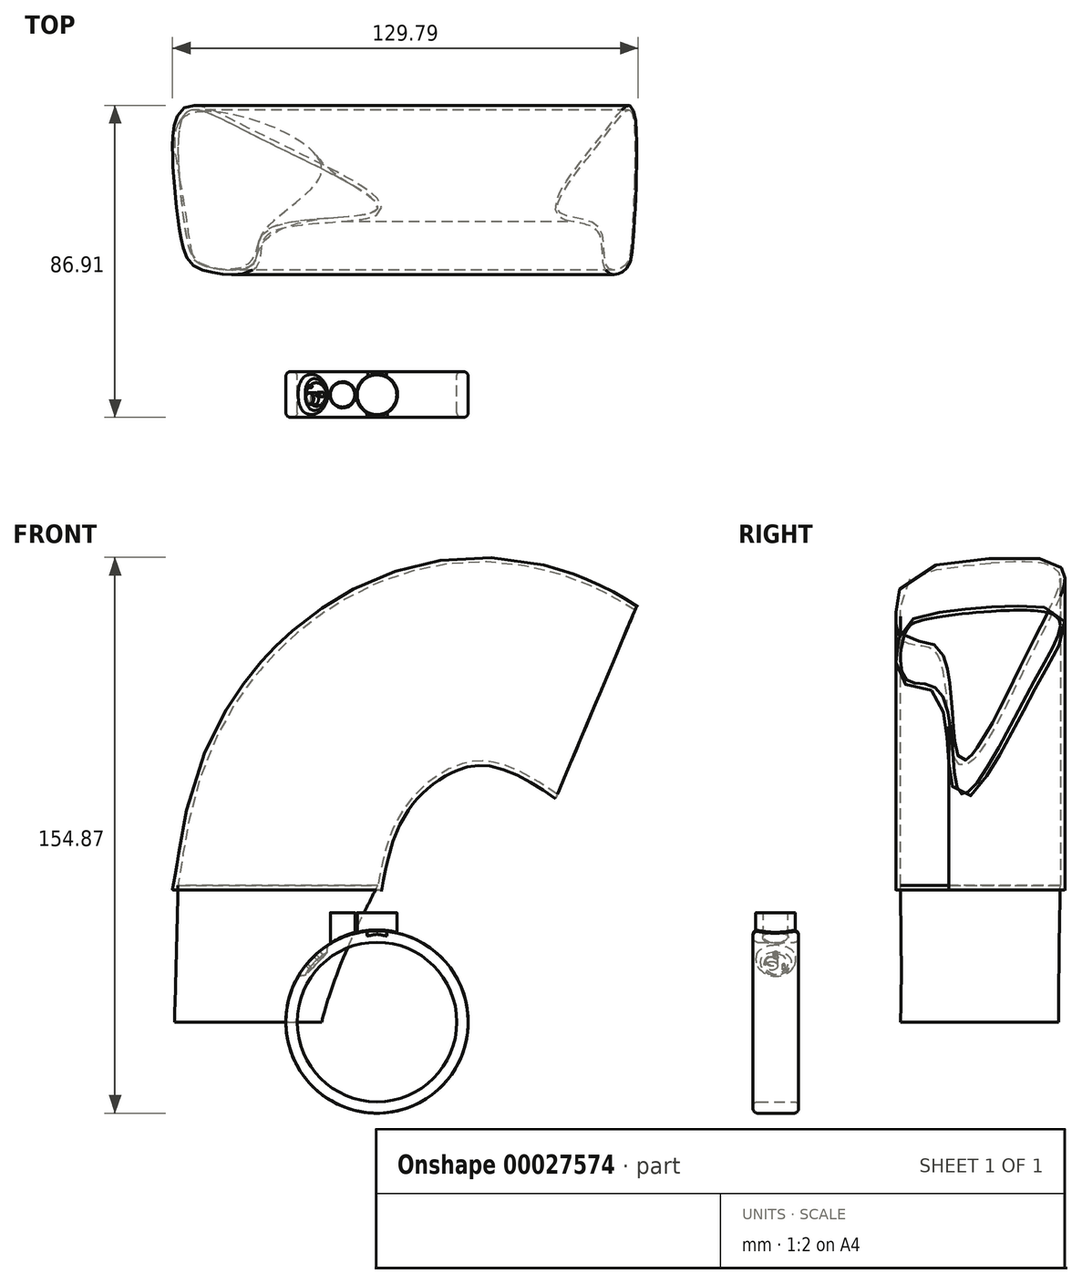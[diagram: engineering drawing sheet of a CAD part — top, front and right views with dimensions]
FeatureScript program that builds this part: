
annotation { "Feature Type Name" : "Feature", "Feature Type Description" : "" }
export const myFeature = defineFeature(function(context is Context, id is Id, definition is map)
    precondition{}
    {
        {
            var Q0;
            Q0=qCreatedBy(makeId("Front.planeOp"),FACE);
            var sketch = newSketch(context, id + "F0", { "sketchPlane" : qUnion([Q0])});
            skCircle(sketch, "E0", {"center": v(0, 0) * mm, "radius": 25.4 * mm});
            skCircle(sketch, "E1", {"center": v(0, 0) * mm, "radius": 22.23 * mm});
            skSolve(sketch);
        }
        {
            var Q0;
            Q0 = qSketchRegion(id + "F0", true);
            extrude(context, id + "F1", {"entities" : qUnion([Q0]), "depth" : 12.7 * mm});
        }
        {
            var Q0;
            Q0=qCreatedBy(makeId("Top.planeOp"),FACE);
            cPlane(context, id + "F2", {"entities" : qUnion([Q0]), "cplaneType" : CPlaneType.OFFSET, "offset" : 30.48 * mm, "width" : 152.4 * mm, "height" : 152.4 * mm});
        }
        {
            var Q0;
            Q0=qCreatedBy(id+"F2.planeOp",FACE);
            var sketch = newSketch(context, id + "F3", { "sketchPlane" : qUnion([Q0])});
            skLineSegment(sketch, "E2", {"start": v(0, -12.85) * mm, "end": v(0, 0) * mm});
            skCircle(sketch, "E3", {"center": v(0, -6.42) * mm, "radius": 5.54 * mm});
            skCircle(sketch, "E4", {"center": v(-9.6, -6.42) * mm, "radius": 3.43 * mm});
            skCircle(sketch, "E5.MirrorC", {"center": v(9.6, -6.42) * mm, "radius": 3.43 * mm});
            skSolve(sketch);
        }
        {
            var Q0;
            Q0=makeQuery(id+"F3.imprint","IMPRINT",FACE,{"disambiguationData":[TD([[makeQuery(id+"F3.imprint","IMPRINT",EDGE,{"derivedFrom":sQuery(id+"F3.wireOp",EDGE,"E4")}),1.0]])]});
            var Q1;
            {var subQ0=sQuery(id+"F3.wireOp",EDGE,"E3");var subQ1=sQuery(id+"F3.wireOp",EDGE,"E2");var subQ3=makeQuery(id+"F3.imprint","INTERSECT",VERTEX,{"disambiguationData":[OD(0.0)],"derivedFrom":[subQ1,subQ0]});Q1=makeQuery(id+"F3.imprint","IMPRINT",FACE,{"disambiguationData":[TD([[makeQuery(id+"F3.imprint","IMPRINT",EDGE,{"disambiguationData":[TD([[subQ3,-1.0]])],"derivedFrom":subQ1}),1.0]])]});}
            var Q2;
            {var subQ0=sQuery(id+"F3.wireOp",EDGE,"E3");var subQ1=sQuery(id+"F3.wireOp",EDGE,"E2");var subQ3=makeQuery(id+"F3.imprint","INTERSECT",VERTEX,{"disambiguationData":[OD(0.0)],"derivedFrom":[subQ1,subQ0]});Q2=makeQuery(id+"F3.imprint","IMPRINT",FACE,{"disambiguationData":[TD([[makeQuery(id+"F3.imprint","IMPRINT",EDGE,{"disambiguationData":[TD([[subQ3,-1.0]])],"derivedFrom":subQ1}),-1.0]])]});}
            var Q3;
            Q3=makeQuery(id+"F3.imprint","IMPRINT",FACE,{"disambiguationData":[TD([[makeQuery(id+"F3.imprint","IMPRINT",EDGE,{"derivedFrom":sQuery(id+"F3.wireOp",EDGE,"E5.MirrorC")}),-1.0]])]});
            var Q4;
            Q4=makeQuery(id+"F1.opExtrude","SWEPT_FACE",FACE,{"disambiguationData":[OSD([sQuery(id+"F0.wireOp",EDGE,"E1")])]});
            extrude(context, id + "F4", {"entities" : qUnion([Q0, Q1, Q2, Q3]), "operationType" : NewBodyOperationType.ADD, "endBound" : BoundingType.UP_TO_SURFACE, "oppositeDirection" : true, "endBoundEntityFace" : qUnion([Q4]), "depth" : 25.4 * mm});
        }
        {
            var Q0;
            Q0=makeQuery(id+"F4.opExtrude","CAP_EDGE",EDGE,{"disambiguationData":[OSD([sQuery(id+"F3.wireOp",EDGE,"E4")])],"isStart":true});
            var Q1;
            Q1=makeQuery(id+"F4.opExtrude","CAP_EDGE",EDGE,{"disambiguationData":[OSD([sQuery(id+"F3.wireOp",EDGE,"E3")])],"isStart":true});
            var Q2;
            Q2=makeQuery(id+"F4.opExtrude","CAP_EDGE",EDGE,{"disambiguationData":[OSD([sQuery(id+"F3.wireOp",EDGE,"E5.MirrorC")])],"isStart":true});
            fillet(context, id + "F5", {"entities" : qUnion([Q0, Q1, Q2]), "radius" : 0.13 * mm, "tangentPropagation" : true, "allowEdgeOverflow" : false});
        }
        {
            var Q0;
            Q0=makeQuery(id+"F4.boolean.opBoolean","INTERSECT",EDGE,{"derivedFrom":[makeQuery(id+"F1.opExtrude","SWEPT_FACE",FACE,{"disambiguationData":[OSD([sQuery(id+"F0.wireOp",EDGE,"E0")])]}),makeQuery(id+"F4.opExtrude","SWEPT_FACE",FACE,{"disambiguationData":[OSD([sQuery(id+"F3.wireOp",EDGE,"E4")])]})]});
            var Q1;
            Q1=makeQuery(id+"F4.boolean.opBoolean","INTERSECT",EDGE,{"derivedFrom":[makeQuery(id+"F1.opExtrude","SWEPT_FACE",FACE,{"disambiguationData":[OSD([sQuery(id+"F0.wireOp",EDGE,"E0")])]}),makeQuery(id+"F4.opExtrude","SWEPT_FACE",FACE,{"disambiguationData":[OSD([sQuery(id+"F3.wireOp",EDGE,"E3")])]})]});
            var Q2;
            Q2=makeQuery(id+"F4.boolean.opBoolean","INTERSECT",EDGE,{"derivedFrom":[makeQuery(id+"F1.opExtrude","SWEPT_FACE",FACE,{"disambiguationData":[OSD([sQuery(id+"F0.wireOp",EDGE,"E0")])]}),makeQuery(id+"F4.opExtrude","SWEPT_FACE",FACE,{"disambiguationData":[OSD([sQuery(id+"F3.wireOp",EDGE,"E5.MirrorC")])]})]});
            chamfer(context, id + "F6", {"entities" : qUnion([Q0, Q1, Q2]), "width" : 0.25 * mm, "tangentPropagation" : true});
        }
        {
            var Q0;
            Q0=makeQuery(id+"F1.opExtrude","CAP_EDGE",EDGE,{"disambiguationData":[OSD([sQuery(id+"F0.wireOp",EDGE,"E0")])],"isStart":false});
            var Q1;
            Q1=makeQuery(id+"F1.opExtrude","CAP_EDGE",EDGE,{"disambiguationData":[OSD([sQuery(id+"F0.wireOp",EDGE,"E1")])],"isStart":false});
            var Q2;
            Q2=makeQuery(id+"F1.opExtrude","CAP_EDGE",EDGE,{"disambiguationData":[OSD([sQuery(id+"F0.wireOp",EDGE,"E1")])],"isStart":true});
            var Q3;
            Q3=makeQuery(id+"F1.opExtrude","CAP_EDGE",EDGE,{"disambiguationData":[OSD([sQuery(id+"F0.wireOp",EDGE,"E0")])],"isStart":true});
            fillet(context, id + "F7", {"entities" : qUnion([Q0, Q1, Q2, Q3]), "radius" : 1.27 * mm, "tangentPropagation" : true, "allowEdgeOverflow" : false});
        }
        {
            var Q0;
            Q0=qCreatedBy(makeId("Front.planeOp"),FACE);
            var sketch = newSketch(context, id + "F8", { "sketchPlane" : qUnion([Q0])});
            skLineSegment(sketch, "E6", {"start": v(-13.03, 30.35) * mm, "end": v(-28.36, 14.3) * mm});
            skSolve(sketch);
        }
        {
            var Q0;
            Q0=sQuery(id+"F8.wireOp",EDGE,"E6");
            cPlane(context, id + "F9", {"entities" : qUnion([Q0]), "cplaneType" : CPlaneType.LINE_ANGLE, "offset" : 152.4 * mm, "angle" : 90 * degree, "width" : 152.4 * mm, "height" : 152.4 * mm});
        }
        {
            var Q0;
            Q0=qCreatedBy(id+"F9.planeOp",FACE);
            var sketch = newSketch(context, id + "F10", { "sketchPlane" : qUnion([Q0])});
            skCircle(sketch, "E7", {"center": v(6.35, 0) * mm, "radius": 4.4 * mm});
            skCircle(sketch, "E8", {"center": v(6.35, 0) * mm, "radius": 3.62 * mm});
            skCircle(sketch, "E9", {"center": v(6.34, 2.52) * mm, "radius": 0.64 * mm});
            skCircle(sketch, "E10", {"center": v(4.12, -2.02) * mm, "radius": 0.34 * mm});
            skCircle(sketch, "E11", {"center": v(7.5, -0.73) * mm, "radius": 1.69 * mm});
            skSolve(sketch);
        }
        {
            var Q0;
            Q0=makeQuery(id+"F10.imprint","IMPRINT",FACE,{"disambiguationData":[TD([[makeQuery(id+"F10.imprint","IMPRINT",EDGE,{"derivedFrom":sQuery(id+"F10.wireOp",EDGE,"E7")}),1.0]])]});
            var Q1;
            Q1=makeQuery(id+"F10.imprint","IMPRINT",FACE,{"disambiguationData":[TD([[makeQuery(id+"F10.imprint","IMPRINT",EDGE,{"derivedFrom":sQuery(id+"F10.wireOp",EDGE,"E8")}),1.0]])]});
            extrude(context, id + "F11", {"entities" : qUnion([Q0, Q1]), "operationType" : NewBodyOperationType.REMOVE, "oppositeDirection" : true, "depth" : 6.97 * mm});
        }
        {
            var Q0;
            Q0=makeQuery(id+"F11.boolean.opBoolean","INTERSECT",EDGE,{"derivedFrom":[makeQuery(id+"F1.opExtrude","SWEPT_FACE",FACE,{"disambiguationData":[OSD([sQuery(id+"F0.wireOp",EDGE,"E0")])]}),makeQuery(id+"F11.opExtrude","SWEPT_FACE",FACE,{"disambiguationData":[OSD([sQuery(id+"F10.wireOp",EDGE,"E7")])]})]});
            chamfer(context, id + "F12", {"entities" : qUnion([Q0]), "width" : 1.27 * mm, "tangentPropagation" : true});
        }
        {
            var Q0;
            Q0=makeQuery(id+"F11.boolean.opBoolean","COPY",EDGE,{"derivedFrom":makeQuery(id+"F11.opExtrude","CAP_EDGE",EDGE,{"disambiguationData":[OSD([sQuery(id+"F10.wireOp",EDGE,"E7")])],"isStart":false})});
            fillet(context, id + "F13", {"entities" : qUnion([Q0]), "radius" : 1.27 * mm, "tangentPropagation" : true, "allowEdgeOverflow" : false});
        }
        {
            var Q0;
            Q0=makeQuery(id+"F11.boolean.opBoolean","INTERSECT",EDGE,{"derivedFrom":[makeQuery(id+"F1.opExtrude","SWEPT_FACE",FACE,{"disambiguationData":[OSD([sQuery(id+"F0.wireOp",EDGE,"E0")])]}),makeQuery(id+"F11.opExtrude","SWEPT_FACE",FACE,{"disambiguationData":[OSD([sQuery(id+"F10.wireOp",EDGE,"E11")])]})]});
            var Q1;
            Q1=makeQuery(id+"F11.boolean.opBoolean","INTERSECT",EDGE,{"derivedFrom":[makeQuery(id+"F1.opExtrude","SWEPT_FACE",FACE,{"disambiguationData":[OSD([sQuery(id+"F0.wireOp",EDGE,"E0")])]}),makeQuery(id+"F11.opExtrude","SWEPT_FACE",FACE,{"disambiguationData":[OSD([sQuery(id+"F10.wireOp",EDGE,"E9")])]})]});
            var Q2;
            Q2=makeQuery(id+"F11.boolean.opBoolean","INTERSECT",EDGE,{"derivedFrom":[makeQuery(id+"F1.opExtrude","SWEPT_FACE",FACE,{"disambiguationData":[OSD([sQuery(id+"F0.wireOp",EDGE,"E0")])]}),makeQuery(id+"F11.opExtrude","SWEPT_FACE",FACE,{"disambiguationData":[OSD([sQuery(id+"F10.wireOp",EDGE,"E10")])]})]});
            fillet(context, id + "F14", {"entities" : qUnion([Q0, Q1, Q2]), "radius" : 0.13 * mm, "tangentPropagation" : true, "allowEdgeOverflow" : false});
        }
        {
            var Q0;
            Q0=qCreatedBy(makeId("Top.planeOp"),FACE);
            var sketch = newSketch(context, id + "F15", { "sketchPlane" : qUnion([Q0])});
            skFitSpline(sketch, "E12", {"points": [v(-54.97, 53.36) * mm, v(-51.94, 34.59) * mm, v(-48.9, 29.84) * mm, v(-34.87, 29.84) * mm, v(-31.46, 39.14) * mm, v(-15.53, 57.53) * mm, v(-52.32, 71.75) * mm, v(-54.97, 53.36) * mm]});
            skSolve(sketch);
        }
        {
            var Q0;
            Q0=qCreatedBy(makeId("Top.planeOp"),FACE);
            cPlane(context, id + "F16", {"entities" : qUnion([Q0]), "cplaneType" : CPlaneType.OFFSET, "offset" : 38.1 * mm, "width" : 152.4 * mm, "height" : 152.4 * mm});
        }
        {
            var Q0;
            Q0=qCreatedBy(id+"F16.planeOp",FACE);
            var sketch = newSketch(context, id + "F17", { "sketchPlane" : qUnion([Q0])});
            skFitSpline(sketch, "E13", {"points": [v(-55.1, 53.7) * mm, v(-52.2, 33.8) * mm, v(-48.48, 29.74) * mm, v(-34.45, 29.96) * mm, v(-30.93, 39.36) * mm, v(0, 45.19) * mm, v(-33.97, 65.64) * mm, v(-53.16, 72.16) * mm, v(-55.1, 53.7) * mm]});
            skPoint(sketch, "E14", {"position": v(-1.38, 48.22) * mm});
            skSolve(sketch);
        }
        {
            var Q0;
            Q0=makeQuery(id+"F17.imprint","IMPRINT",FACE,{"disambiguationData":[TD([[makeQuery(id+"F17.imprint","IMPRINT",EDGE,{"derivedFrom":sQuery(id+"F17.wireOp",EDGE,"E13")}),1.0]])]});
            var Q1;
            Q1=makeQuery(id+"F15.imprint","IMPRINT",FACE,{"disambiguationData":[TD([[makeQuery(id+"F15.imprint","IMPRINT",EDGE,{"derivedFrom":sQuery(id+"F15.wireOp",EDGE,"E12")}),1.0]])]});
            loft(context, id + "F18", {"sheetProfilesArray" : [{ "sheetProfileEntities" : qUnion([Q0]) }, { "sheetProfileEntities" : qUnion([Q1]) }]});
        }
        {
            var Q0;
            Q0=makeQuery(id+"F18.opLoft","CAP_FACE",FACE,{"disambiguationData":[OSD([makeQuery(id+"F17.imprint","IMPRINT",FACE,{"disambiguationData":[TD([[makeQuery(id+"F17.imprint","IMPRINT",EDGE,{"derivedFrom":sQuery(id+"F17.wireOp",EDGE,"E13")}),1.0]])]})])],"isStart":true});
            var sketch = newSketch(context, id + "F19", { "sketchPlane" : qUnion([Q0])});
            skPoint(sketch, "E15", {"position": v(0.22, 45.7) * mm});
            skSolve(sketch);
        }
        {
            var Q0;
            Q0=qCreatedBy(makeId("Front.planeOp"),FACE);
            var Q1;
            Q1=sQuery(id+"F19.wireOp",VERTEX,"E15");
            cPlane(context, id + "F20", {"entities" : qUnion([Q0, Q1]), "cplaneType" : CPlaneType.PLANE_POINT, "offset" : 152.4 * mm, "width" : 152.4 * mm, "height" : 152.4 * mm});
        }
        {
            var Q0;
            Q0=qCreatedBy(id+"F20.planeOp",FACE);
            var sketch = newSketch(context, id + "F21", { "sketchPlane" : qUnion([Q0])});
            skFitSpline(sketch, "E16", {"points": [v(0.22, 38.1) * mm, v(7.6, 59.62) * mm, v(27.88, 72.72) * mm, v(50.28, 63.42) * mm], "startDerivative": vector(13.05, 68.64) * mm, "endDerivative": vector(65.53, -43.53) * mm});
            skSolve(sketch);
        }
        {
            var Q0;
            Q0=makeQuery(id+"F19.imprint","IMPRINT",FACE,{"disambiguationData":[TD([[makeQuery(id+"F19.imprint","IMPRINT",EDGE,{"derivedFrom":makeQuery(id+"F18.opLoft","MID_CAP_EDGE",EDGE,{"disambiguationData":[OSD([sQuery(id+"F17.wireOp",EDGE,"E13")])],"capPos":0.0})}),1.0]])]});
            var Q1;
            Q1=sQuery(id+"F21.wireOp",EDGE,"E16");
            sweep(context, id + "F22", {"profiles" : qUnion([Q0]), "path" : qUnion([Q1])});
        }
        {
            var Q0;
            Q0=makeQuery(id+"F22.opSweep","CAP_FACE",FACE,{"disambiguationData":[OSD([sQuery(id+"F17.wireOp",EDGE,"E13"),sQuery(id+"F21.wireOp",VERTEX,"E16.end")])],"isStart":false});
            var Q1;
            Q1=makeQuery(id+"F22.opSweep","SWEPT_BODY",BODY,{"disambiguationData":[OSD([sQuery(id+"F17.wireOp",EDGE,"E13"),sQuery(id+"F21.wireOp",EDGE,"E16")])]});
            shell(context, id + "F23", {"entities" : qUnion([Q0]), "parts" : qUnion([Q1]), "thickness" : 1.27 * mm, "oppositeDirection" : true});
        }
    });
